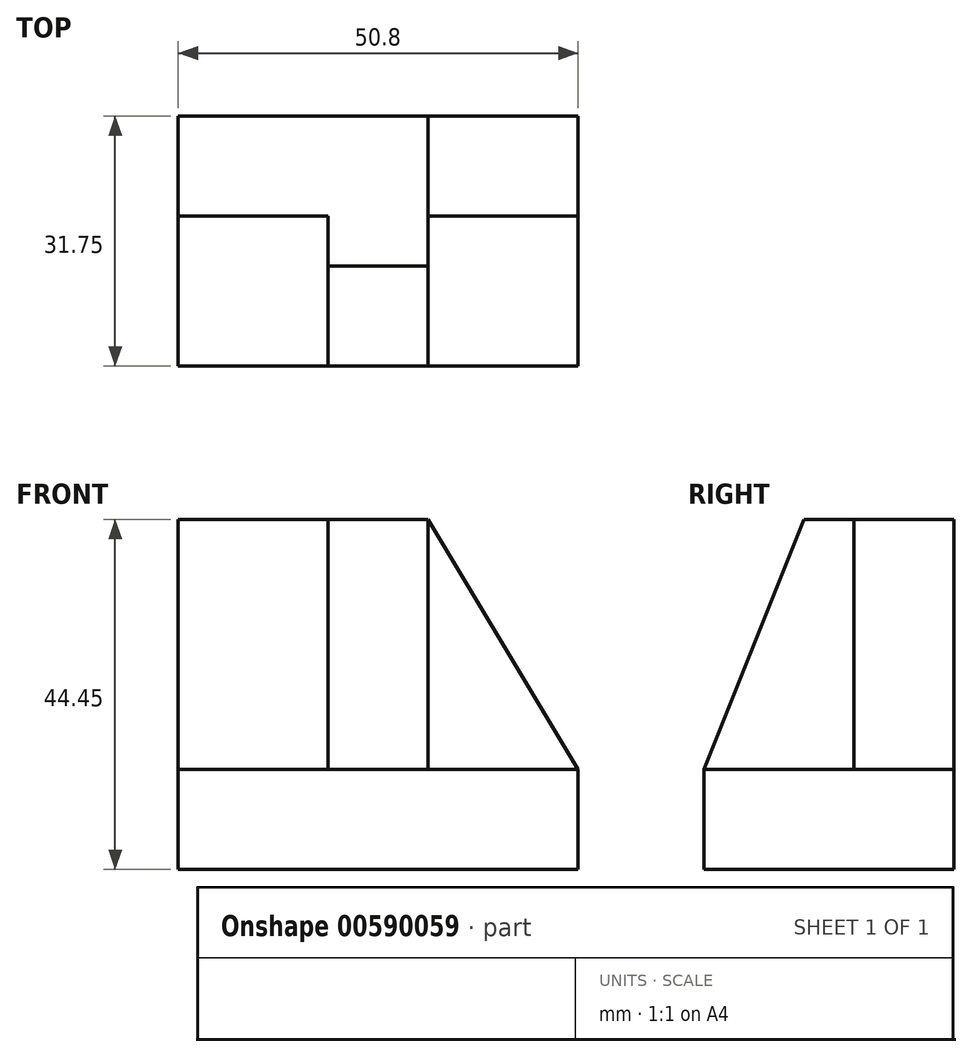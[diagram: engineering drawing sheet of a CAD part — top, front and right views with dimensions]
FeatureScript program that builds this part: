
annotation { "Feature Type Name" : "Feature", "Feature Type Description" : "" }
export const myFeature = defineFeature(function(context is Context, id is Id, definition is map)
    precondition{}
    {
        {
            var Q0;
            Q0=qCreatedBy(makeId("Front.planeOp"),FACE);
            var sketch = newSketch(context, id + "F0", { "sketchPlane" : qUnion([Q0])});
            skLineSegment(sketch, "E0", {"start": v(-69.43, 61.67) * mm, "end": v(-18.63, 61.67) * mm});
            skLineSegment(sketch, "E1", {"start": v(-18.63, 61.67) * mm, "end": v(-18.63, 17.22) * mm});
            skLineSegment(sketch, "E2", {"start": v(-18.63, 17.22) * mm, "end": v(-69.43, 17.22) * mm});
            skLineSegment(sketch, "E3", {"start": v(-69.43, 61.67) * mm, "end": v(-69.43, 17.22) * mm});
            skSolve(sketch);
        }
        {
            var Q0;
            Q0=makeQuery(id+"F0.imprint","IMPRINT",FACE,{"disambiguationData":[TD([[makeQuery(id+"F0.imprint","IMPRINT",EDGE,{"derivedFrom":sQuery(id+"F0.wireOp",EDGE,"E0")}),-1.0]])]});
            extrude(context, id + "F1", {"entities" : qUnion([Q0]), "depth" : 31.75 * mm, "offsetDistance" : 25.4 * mm});
        }
        {
            var Q0;
            Q0=makeQuery(id+"F1.opExtrude","SWEPT_FACE",FACE,{"disambiguationData":[OSD([sQuery(id+"F0.wireOp",EDGE,"E1")])]});
            var sketch = newSketch(context, id + "F2", { "sketchPlane" : qUnion([Q0])});
            skLineSegment(sketch, "E4", {"start": v(-12.7, 61.67) * mm, "end": v(-12.7, 29.92) * mm});
            skLineSegment(sketch, "E5", {"start": v(-12.7, 29.92) * mm, "end": v(-31.75, 29.92) * mm});
            skSolve(sketch);
        }
        {
            var Q0;
            {var subQ0=sQuery(id+"F2.wireOp",EDGE,"E4");Q0=makeQuery(id+"F2.imprint","IMPRINT",FACE,{"disambiguationData":[TD([[makeQuery(id+"F2.imprint","IMPRINT",EDGE,{"derivedFrom":subQ0}),-1.0]])]});}
            extrude(context, id + "F3", {"entities" : qUnion([Q0]), "operationType" : NewBodyOperationType.REMOVE, "oppositeDirection" : true, "depth" : 19.05 * mm, "offsetDistance" : 25.4 * mm});
        }
        {
            var Q0;
            Q0=makeQuery(id+"F1.opExtrude","CAP_FACE",FACE,{"disambiguationData":[OSD([sQuery(id+"F0.wireOp",EDGE,"E0"),sQuery(id+"F0.wireOp",EDGE,"E1"),sQuery(id+"F0.wireOp",EDGE,"E2"),sQuery(id+"F0.wireOp",EDGE,"E3")])],"isStart":true});
            var sketch = newSketch(context, id + "F4", { "sketchPlane" : qUnion([Q0])});
            skLineSegment(sketch, "E6", {"start": v(37.68, 61.67) * mm, "end": v(18.63, 29.92) * mm});
            skSolve(sketch);
        }
        {
            var Q0;
            {var subQ0=sQuery(id+"F4.wireOp",EDGE,"E6");Q0=makeQuery(id+"F4.imprint","IMPRINT",FACE,{"disambiguationData":[TD([[makeQuery(id+"F4.imprint","IMPRINT",EDGE,{"derivedFrom":subQ0}),-1.0]])]});}
            extrude(context, id + "F5", {"entities" : qUnion([Q0]), "operationType" : NewBodyOperationType.REMOVE, "oppositeDirection" : true, "depth" : 12.7 * mm, "offsetDistance" : 25.4 * mm});
        }
        {
            var Q0;
            Q0=makeQuery(id+"F3.boolean.opBoolean","COPY",FACE,{"derivedFrom":makeQuery(id+"F3.opExtrude","CAP_FACE",FACE,{"disambiguationData":[OSD([sQuery(id+"F0.wireOp",EDGE,"E0"),sQuery(id+"F0.wireOp",EDGE,"E1"),sQuery(id+"F2.wireOp",EDGE,"E4"),sQuery(id+"F2.wireOp",EDGE,"E5")])],"isStart":false})});
            var sketch = newSketch(context, id + "F6", { "sketchPlane" : qUnion([Q0])});
            skLineSegment(sketch, "E7", {"start": v(-19.05, 61.67) * mm, "end": v(-31.75, 29.92) * mm});
            skSolve(sketch);
        }
        {
            var Q0;
            {var subQ0=sQuery(id+"F6.wireOp",EDGE,"E7");Q0=makeQuery(id+"F6.imprint","IMPRINT",FACE,{"disambiguationData":[TD([[makeQuery(id+"F6.imprint","IMPRINT",EDGE,{"derivedFrom":subQ0}),-1.0]])]});}
            extrude(context, id + "F7", {"entities" : qUnion([Q0]), "operationType" : NewBodyOperationType.REMOVE, "oppositeDirection" : true, "depth" : 12.7 * mm, "offsetDistance" : 25.4 * mm});
        }
        {
            var Q0;
            Q0=makeQuery(id+"F1.opExtrude","SWEPT_FACE",FACE,{"disambiguationData":[OSD([sQuery(id+"F0.wireOp",EDGE,"E3")])]});
            var sketch = newSketch(context, id + "F8", { "sketchPlane" : qUnion([Q0])});
            skLineSegment(sketch, "E8", {"start": v(12.7, 61.67) * mm, "end": v(12.7, 29.92) * mm});
            skLineSegment(sketch, "E9", {"start": v(12.7, 29.92) * mm, "end": v(31.75, 29.92) * mm});
            skSolve(sketch);
        }
        {
            var Q0;
            {var subQ0=sQuery(id+"F8.wireOp",EDGE,"E8");Q0=makeQuery(id+"F8.imprint","IMPRINT",FACE,{"disambiguationData":[TD([[makeQuery(id+"F8.imprint","IMPRINT",EDGE,{"derivedFrom":subQ0}),1.0]])]});}
            extrude(context, id + "F9", {"entities" : qUnion([Q0]), "operationType" : NewBodyOperationType.REMOVE, "oppositeDirection" : true, "depth" : 19.05 * mm, "offsetDistance" : 25.4 * mm});
        }
    });
